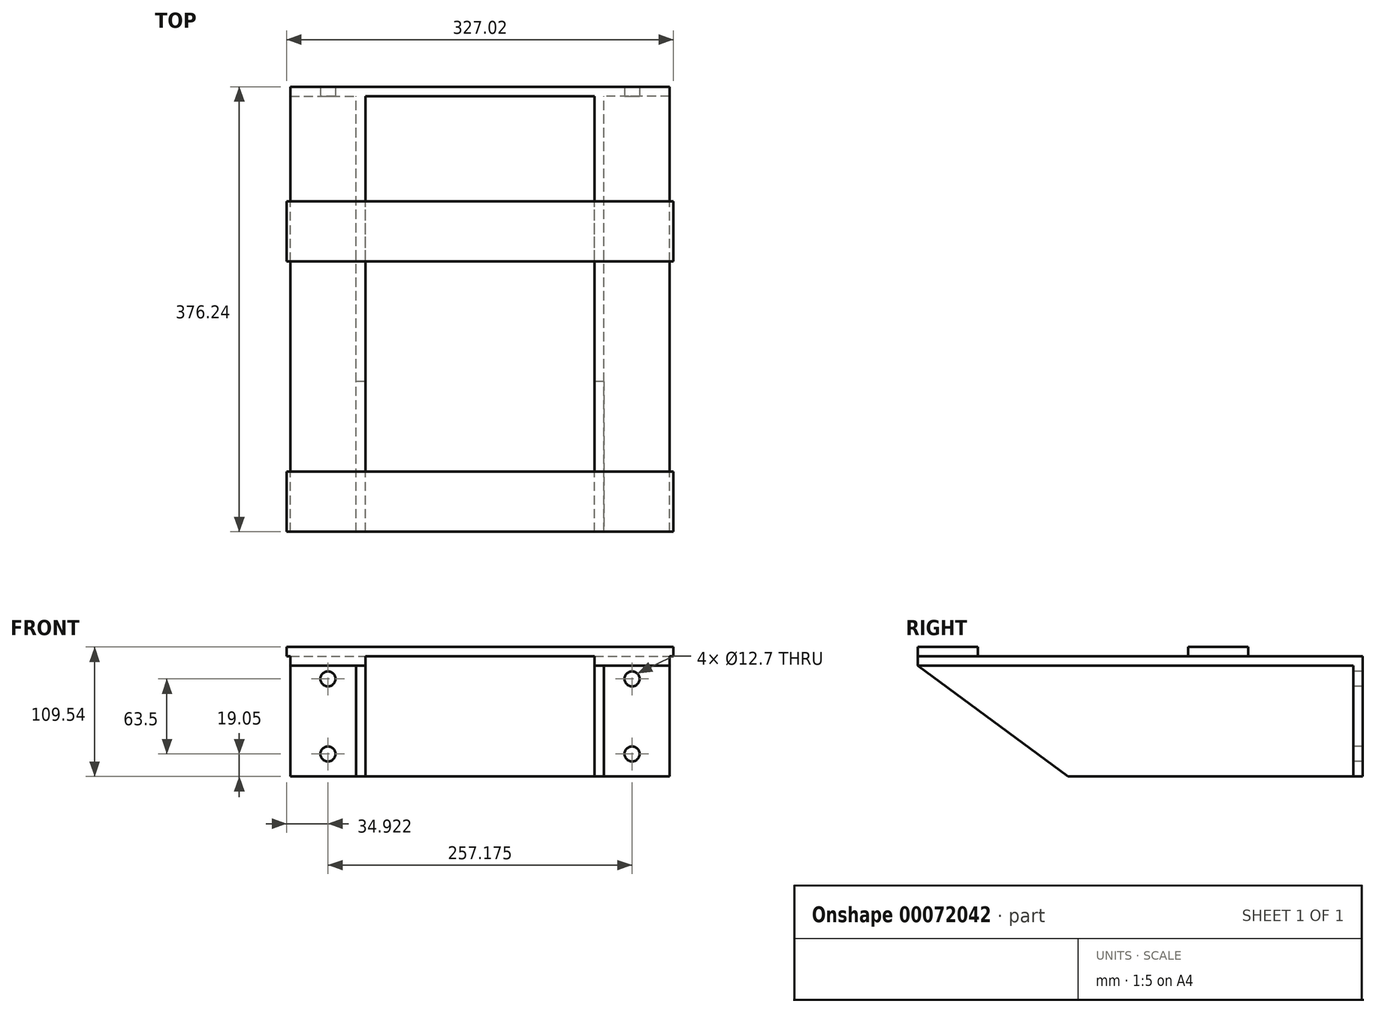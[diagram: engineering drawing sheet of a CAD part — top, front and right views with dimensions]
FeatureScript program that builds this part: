
annotation { "Feature Type Name" : "Feature", "Feature Type Description" : "" }
export const myFeature = defineFeature(function(context is Context, id is Id, definition is map)
    precondition{}
    {
        {
            var Q0;
            Q0=qCreatedBy(makeId("Front.planeOp"),FACE);
            var sketch = newSketch(context, id + "F0", { "sketchPlane" : qUnion([Q0])});
            skLineSegment(sketch, "E0.bottom", {"start": v(-160.34, 0) * mm, "end": v(160.34, 0) * mm});
            skLineSegment(sketch, "E0.top", {"start": v(-160.34, -101.6) * mm, "end": v(160.34, -101.6) * mm});
            skLineSegment(sketch, "E0.left", {"start": v(-160.34, 0) * mm, "end": v(-160.34, -101.6) * mm});
            skLineSegment(sketch, "E0.right", {"start": v(160.34, 0) * mm, "end": v(160.34, -101.6) * mm});
            skSolve(sketch);
        }
        {
            var Q0;
            Q0=makeQuery(id+"F0.imprint","IMPRINT",FACE,{"disambiguationData":[TD([[makeQuery(id+"F0.imprint","IMPRINT",EDGE,{"derivedFrom":sQuery(id+"F0.wireOp",EDGE,"E0.bottom")}),-1.0]])]});
            extrude(context, id + "F1", {"entities" : qUnion([Q0]), "depth" : 7.94 * mm});
        }
        {
            var Q0;
            Q0=makeQuery(id+"F1.opExtrude","CAP_FACE",FACE,{"disambiguationData":[OSD([sQuery(id+"F0.wireOp",EDGE,"E0.bottom"),sQuery(id+"F0.wireOp",EDGE,"E0.top"),sQuery(id+"F0.wireOp",EDGE,"E0.left"),sQuery(id+"F0.wireOp",EDGE,"E0.right")])],"isStart":false});
            var sketch = newSketch(context, id + "F2", { "sketchPlane" : qUnion([Q0])});
            skLineSegment(sketch, "E1.bottom", {"start": v(-128.59, -19.05) * mm, "end": v(128.59, -19.05) * mm});
            skLineSegment(sketch, "E1.top", {"start": v(-128.59, -82.55) * mm, "end": v(128.59, -82.55) * mm});
            skLineSegment(sketch, "E1.left", {"start": v(-128.59, -19.05) * mm, "end": v(-128.59, -82.55) * mm});
            skLineSegment(sketch, "E1.right", {"start": v(128.59, -19.05) * mm, "end": v(128.59, -82.55) * mm});
            skSolve(sketch);
        }
        {
            var Q0;
            Q0=sQuery(id+"F2.wireOp",VERTEX,"E1.left.start");
            var Q1;
            Q1=sQuery(id+"F2.wireOp",VERTEX,"E1.right.start");
            var Q2;
            Q2=sQuery(id+"F2.wireOp",VERTEX,"E1.top.end");
            var Q3;
            Q3=sQuery(id+"F2.wireOp",VERTEX,"E1.left.end");
            var Q4;
            Q4=makeQuery(id+"F1.opExtrude","SWEPT_BODY",BODY,{"disambiguationData":[OSD([sQuery(id+"F0.wireOp",EDGE,"E0.bottom"),sQuery(id+"F0.wireOp",EDGE,"E0.top"),sQuery(id+"F0.wireOp",EDGE,"E0.left"),sQuery(id+"F0.wireOp",EDGE,"E0.right")])]});
            hole(context, id + "F3", {"style" : HoleStyle.SIMPLE, "holeDiameter" : 12.7 * mm, "endStyle" : HoleEndStyle.THROUGH, "locations" : qUnion([Q0, Q1, Q2, Q3]), "scope" : qUnion([Q4])});
        }
        {
            var Q0;
            Q0=makeQuery(id+"F1.opExtrude","CAP_FACE",FACE,{"disambiguationData":[OSD([sQuery(id+"F0.wireOp",EDGE,"E0.bottom"),sQuery(id+"F0.wireOp",EDGE,"E0.top"),sQuery(id+"F0.wireOp",EDGE,"E0.left"),sQuery(id+"F0.wireOp",EDGE,"E0.right")])],"isStart":false});
            var sketch = newSketch(context, id + "F4", { "sketchPlane" : qUnion([Q0])});
            skLineSegment(sketch, "E2", {"start": v(-160.34, 0) * mm, "end": v(-160.34, -7.94) * mm});
            skLineSegment(sketch, "E3", {"start": v(-160.34, -7.94) * mm, "end": v(-104.78, -7.94) * mm});
            skLineSegment(sketch, "E4", {"start": v(-104.78, -7.94) * mm, "end": v(-104.78, -101.6) * mm});
            skLineSegment(sketch, "E5", {"start": v(-104.78, -101.6) * mm, "end": v(-96.84, -101.6) * mm});
            skLineSegment(sketch, "E6", {"start": v(-96.84, -101.6) * mm, "end": v(-96.84, 0) * mm});
            skLineSegment(sketch, "E7", {"start": v(-96.84, 0) * mm, "end": v(-160.34, 0) * mm});
            skLineSegment(sketch, "E8.MirrorCS", {"start": v(96.84, 0) * mm, "end": v(160.34, 0) * mm});
            skLineSegment(sketch, "E9.MirrorCS", {"start": v(160.34, -7.94) * mm, "end": v(104.78, -7.94) * mm});
            skLineSegment(sketch, "E10.MirrorCS", {"start": v(96.84, -101.6) * mm, "end": v(96.84, 0) * mm});
            skLineSegment(sketch, "E11.MirrorCS", {"start": v(104.78, -7.94) * mm, "end": v(104.78, -101.6) * mm});
            skLineSegment(sketch, "E12.MirrorCS", {"start": v(104.78, -101.6) * mm, "end": v(96.84, -101.6) * mm});
            skLineSegment(sketch, "E13.MirrorCS", {"start": v(160.34, 0) * mm, "end": v(160.34, -7.94) * mm});
            skSolve(sketch);
        }
        {
            var Q0;
            Q0=qSketchRegion(id+"F4",true);
            extrude(context, id + "F5", {"entities" : qUnion([Q0]), "operationType" : NewBodyOperationType.ADD, "depth" : 368.3 * mm});
        }
        {
            var Q0;
            Q0=makeQuery(id+"F5.opExtrude","SWEPT_FACE",FACE,{"disambiguationData":[OSD([sQuery(id+"F4.wireOp",EDGE,"E4")])]});
            var sketch = newSketch(context, id + "F6", { "sketchPlane" : qUnion([Q0])});
            skLineSegment(sketch, "E14", {"start": v(376.24, -7.94) * mm, "end": v(249.24, -101.6) * mm});
            skLineSegment(sketch, "E15", {"start": v(249.24, -101.6) * mm, "end": v(376.24, -101.6) * mm});
            skLineSegment(sketch, "E16", {"start": v(376.24, -101.6) * mm, "end": v(376.24, -7.94) * mm});
            skSolve(sketch);
        }
        {
            var Q0;
            Q0=qSketchRegion(id+"F6",true);
            extrude(context, id + "F7", {"entities" : qUnion([Q0]), "operationType" : NewBodyOperationType.REMOVE, "endBound" : BoundingType.THROUGH_ALL, "oppositeDirection" : true, "depth" : 25.4 * mm});
        }
        {
            var Q0;
            Q0=makeQuery(id+"F5.boolean.opBoolean","MERGE",FACE,{"derivedFrom":[makeQuery(id+"F1.opExtrude","SWEPT_FACE",FACE,{"disambiguationData":[OSD([sQuery(id+"F0.wireOp",EDGE,"E0.bottom")])]}),makeQuery(id+"F5.opExtrude","SWEPT_FACE",FACE,{"disambiguationData":[OSD([sQuery(id+"F4.wireOp",EDGE,"E7")])]}),makeQuery(id+"F5.opExtrude","SWEPT_FACE",FACE,{"disambiguationData":[OSD([sQuery(id+"F4.wireOp",EDGE,"E8.MirrorCS")])]})]});
            var sketch = newSketch(context, id + "F8", { "sketchPlane" : qUnion([Q0])});
            skLineSegment(sketch, "E17.bottom", {"start": v(-163.51, -96.84) * mm, "end": v(163.51, -96.84) * mm});
            skLineSegment(sketch, "E17.top", {"start": v(-163.51, -147.64) * mm, "end": v(163.51, -147.64) * mm});
            skLineSegment(sketch, "E17.left", {"start": v(-163.51, -96.84) * mm, "end": v(-163.51, -147.64) * mm});
            skLineSegment(sketch, "E17.right", {"start": v(163.51, -96.84) * mm, "end": v(163.51, -147.64) * mm});
            skLineSegment(sketch, "E18.bottom", {"start": v(-163.51, -325.44) * mm, "end": v(163.51, -325.44) * mm});
            skLineSegment(sketch, "E18.top", {"start": v(-163.51, -376.24) * mm, "end": v(163.51, -376.24) * mm});
            skLineSegment(sketch, "E18.left", {"start": v(-163.51, -325.44) * mm, "end": v(-163.51, -376.24) * mm});
            skLineSegment(sketch, "E18.right", {"start": v(163.51, -325.44) * mm, "end": v(163.51, -376.24) * mm});
            skSolve(sketch);
        }
        {
            var Q0;
            Q0=qSketchRegion(id+"F8",true);
            extrude(context, id + "F9", {"entities" : qUnion([Q0]), "operationType" : NewBodyOperationType.ADD, "depth" : 7.94 * mm});
        }
    });
